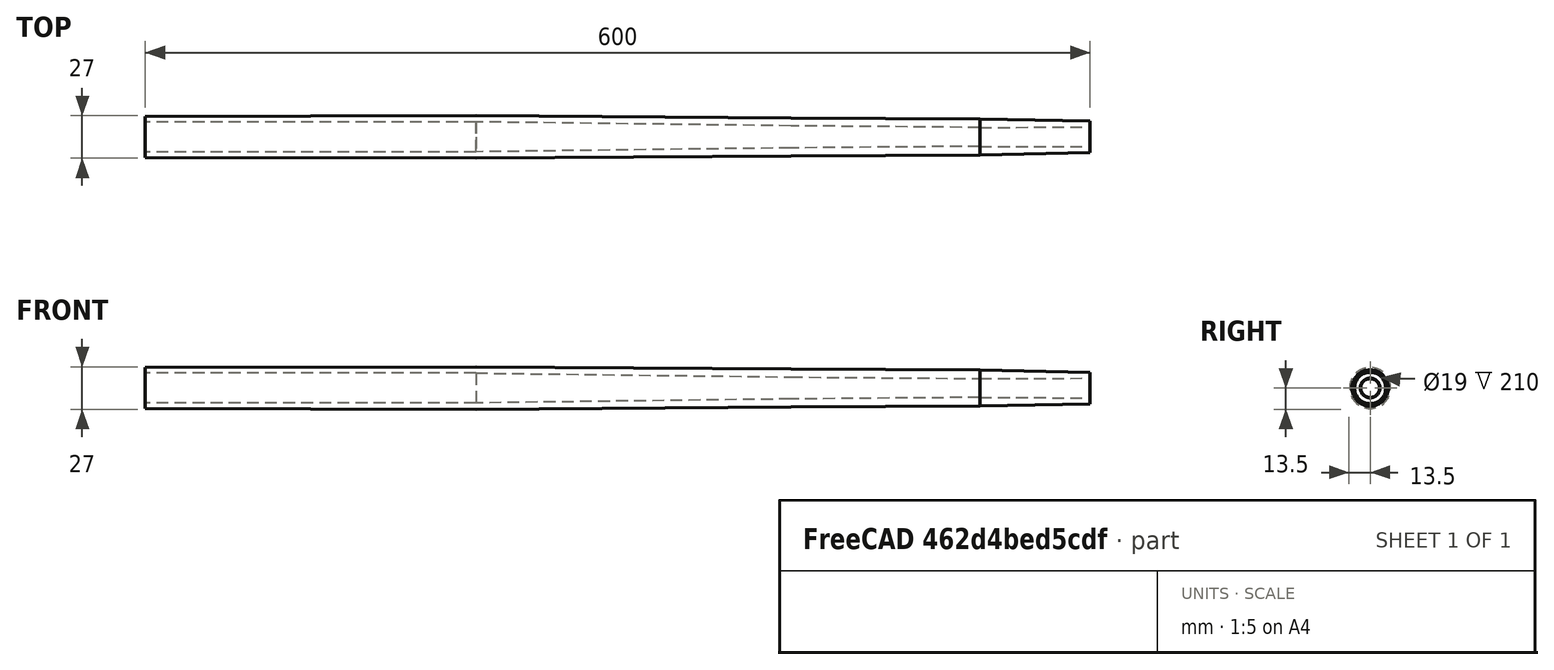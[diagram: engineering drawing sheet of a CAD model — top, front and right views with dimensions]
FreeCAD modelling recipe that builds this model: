
FCSTD DOCUMENT  (FreeCAD 1.0R39319 (Git))
Label: flut
License: All rights reserved
objects: Sketcher::SketchObject×1, PartDesign::Revolution×1, PartDesign::Body×1
note: 6 computed .brp shape members not serialized (recipe doc carries the construction recipe); baked Part::Feature solids carry a one-line shape summary decoded from their .brp

FEATURE [Sketcher::SketchObject] Sketch
  ArcFitTolerance = 1e-06
  AttachmentSupport = -> [XZ_Plane]
  FullyConstrained = true
  MakeInternals = false
  MapMode = 5
  Placement = pos=(0,0,0) rot=(1,0,0;1.5708rad)
  sketch-geometry (15):
    g0: GeomPoint X=0 Y=9.5 Z=0
    g1: GeomPoint X=210 Y=9.5 Z=0
    g2: GeomPoint X=410 Y=7 Z=0
    g3: GeomPoint X=530 Y=6 Z=0
    g4: GeomPoint X=600 Y=6.25 Z=0
    g5: LineSegment StartX=210 StartY=9.5 StartZ=0 EndX=0 EndY=9.5 EndZ=0
    g6: LineSegment StartX=210 StartY=9.5 StartZ=0 EndX=410 EndY=7 EndZ=0
    g7: LineSegment StartX=410 StartY=7 StartZ=0 EndX=530 EndY=6 EndZ=0
    g8: LineSegment StartX=530 StartY=6 StartZ=0 EndX=600 EndY=6.25 EndZ=0
    g9: LineSegment StartX=0 StartY=13 StartZ=0 EndX=210 EndY=13.5 EndZ=0
    g10: LineSegment StartX=210 StartY=13.5 StartZ=0 EndX=410 EndY=12 EndZ=0
    g11: LineSegment StartX=410 StartY=12 StartZ=0 EndX=530 EndY=11.5 EndZ=0
    g12: LineSegment StartX=530 StartY=11.5 StartZ=0 EndX=600 EndY=10 EndZ=0
    g13: LineSegment StartX=600 StartY=10 StartZ=0 EndX=600 EndY=6.25 EndZ=0
    g14: LineSegment StartX=0 StartY=13 StartZ=0 EndX=0 EndY=9.5 EndZ=0
  constraints (36):
    c: DistanceY(g-1,g0) = 9.5
    c: DistanceY(g-1,g1) = 9.5
    c: DistanceY(g-1,g2) = 7
    c: DistanceY(g-1,g3) = 6
    c: DistanceY(g-1,g4) = 6.25
    c: DistanceX(g-1,g0) = 0
    c: DistanceX(g-1,g1) = 210
    c: DistanceX(g-1,g2) = 410
    c: DistanceX(g-1,g3) = 530
    c: DistanceX(g-1,g4) = 600
    c: Coincident(g5,g1)
    c: Coincident(g5,g0)
    c: Coincident(g6,g1)
    c: Coincident(g6,g2)
    c: Coincident(g7,g2)
    c: Coincident(g7,g3)
    c: Coincident(g8,g3)
    c: Coincident(g8,g4)
    c: Coincident(g9,g10)
    c: Coincident(g10,g11)
    c: Coincident(g11,g12)
    c: Coincident(g12,g13)
    c: DistanceX(g9,g1) = 0
    c: DistanceX(g10,g2) = 0
    c: DistanceX(g11,g3) = 0
    c: Coincident(g13,g4)
    c: DistanceX(g12,g4) = 0
    c: Coincident(g14,g9)
    c: PointOnObject(g14,g-2)
    c: DistanceY(g-1,g14) = 9.5
    c: DistanceY(g-1,g9) = 13
    c: DistanceX(g9,g-1) = 0
    c: DistanceY(g-1,g10) = 12
    c: DistanceY(g3,g11) = 5.5
    c: DistanceY(g13,g13) = 3.75
    c: DistanceY(g1,g9) = 4
FEATURE [PartDesign::Revolution] Revolution
  Angle = 360
  Angle2 = 60
  Axis = (1,0,0)
  Base = (0,0,0)
  Placement = pos=(0,0,0) rot=(1,0,0;1.5708rad)
  Profile = -> Sketch
  ReferenceAxis = -> X_Axis
  Refine = true
  Suppressed = false
  Type = 0
FEATURE [PartDesign::Body] Body
  AllowCompound = false
  Group = -> [Sketch,Revolution]
  Origin = -> Origin
  Tip = -> Revolution
